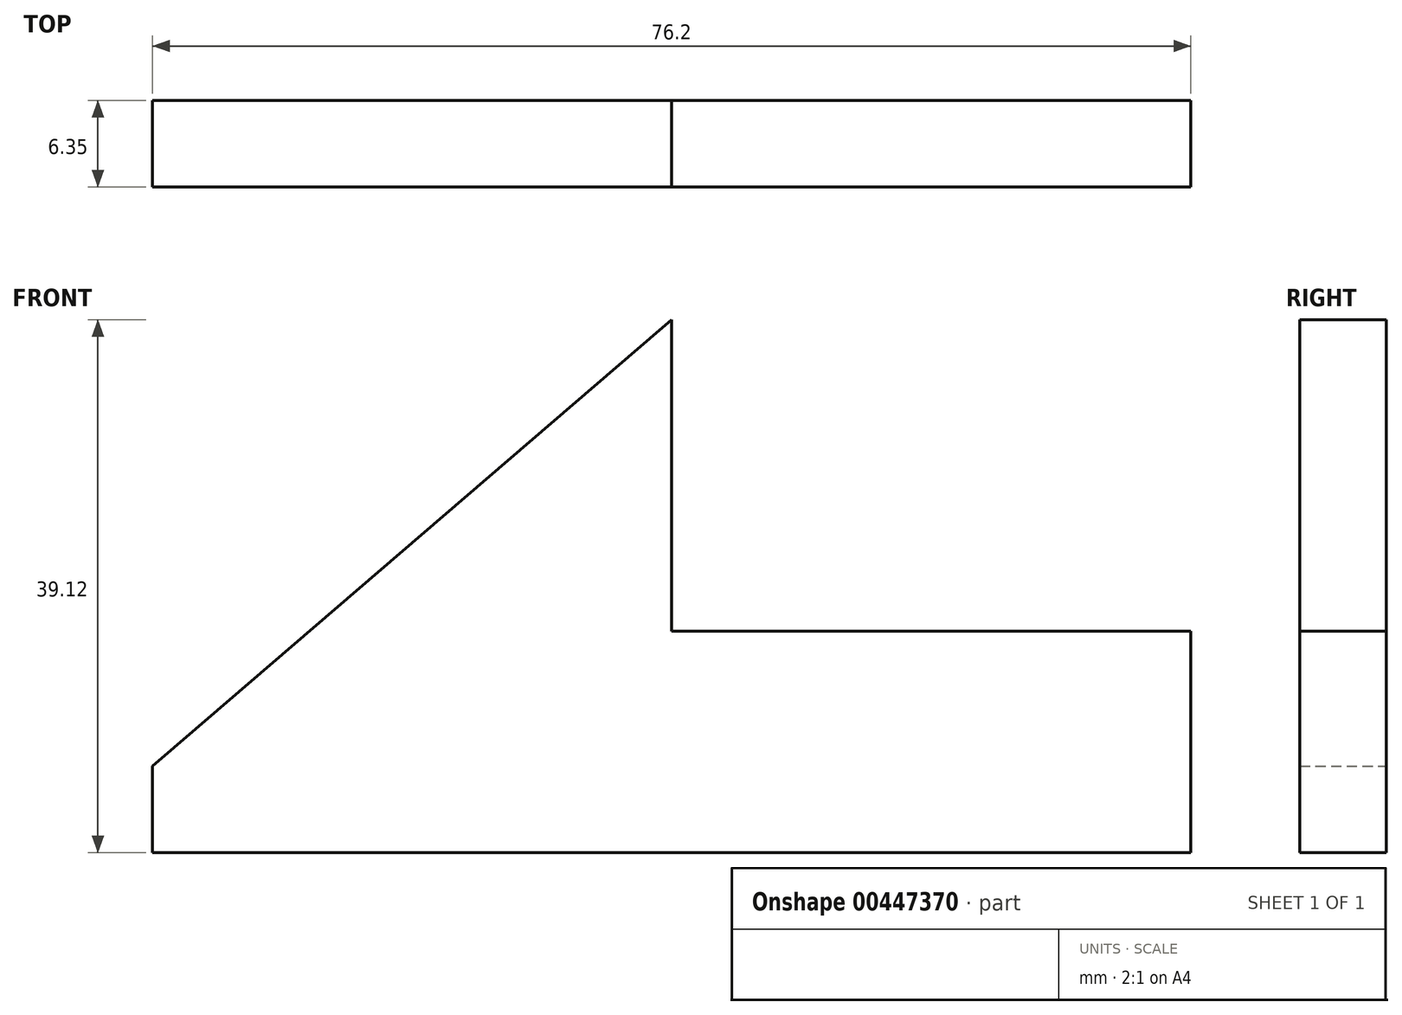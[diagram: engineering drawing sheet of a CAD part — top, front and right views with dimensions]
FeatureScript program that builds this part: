
annotation { "Feature Type Name" : "Feature", "Feature Type Description" : "" }
export const myFeature = defineFeature(function(context is Context, id is Id, definition is map)
    precondition{}
    {
        {
            var Q0;
            Q0=qCreatedBy(makeId("Front.planeOp"),FACE);
            var sketch = newSketch(context, id + "F0", { "sketchPlane" : qUnion([Q0])});
            skLineSegment(sketch, "E0", {"start": v(-38.1, 34.68) * mm, "end": v(-38.1, 28.33) * mm});
            skLineSegment(sketch, "E1.bottom", {"start": v(0, 0) * mm, "end": v(38.1, 0) * mm});
            skLineSegment(sketch, "E1.top", {"start": v(0, 16.26) * mm, "end": v(38.1, 16.26) * mm});
            skLineSegment(sketch, "E1.left", {"start": v(0, 0) * mm, "end": v(0, 16.26) * mm});
            skLineSegment(sketch, "E1.right", {"start": v(38.1, 0) * mm, "end": v(38.1, 16.26) * mm});
            skLineSegment(sketch, "E2.bottom", {"start": v(0, 0) * mm, "end": v(-38.1, 0) * mm});
            skLineSegment(sketch, "E2.top", {"start": v(0, 39.12) * mm, "end": v(-38.1, 39.12) * mm});
            skLineSegment(sketch, "E2.left", {"start": v(0, 0) * mm, "end": v(0, 39.12) * mm});
            skLineSegment(sketch, "E2.right", {"start": v(-38.1, 0) * mm, "end": v(-38.1, 39.12) * mm});
            skLineSegment(sketch, "E3", {"start": v(-38.1, 0) * mm, "end": v(-38.1, 6.35) * mm});
            skLineSegment(sketch, "E4", {"start": v(0, 39.12) * mm, "end": v(-38.1, 6.35) * mm});
            skSolve(sketch);
        }
        {
            var Q0;
            {var subQ0=sQuery(id+"F0.wireOp",EDGE,"E1.bottom");Q0=makeQuery(id+"F0.imprint","IMPRINT",FACE,{"disambiguationData":[TD([[makeQuery(id+"F0.imprint","IMPRINT",EDGE,{"derivedFrom":subQ0}),1.0]])]});}
            var Q1;
            {var subQ3=sQuery(id+"F0.wireOp",EDGE,"E2.bottom");Q1=makeQuery(id+"F0.imprint","IMPRINT",FACE,{"disambiguationData":[TD([[makeQuery(id+"F0.imprint","IMPRINT",EDGE,{"derivedFrom":subQ3}),-1.0]])]});}
            extrude(context, id + "F1", {"entities" : qUnion([Q0, Q1]), "depth" : 6.35 * mm});
        }
    });
